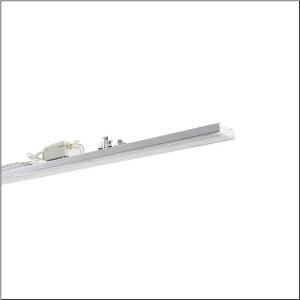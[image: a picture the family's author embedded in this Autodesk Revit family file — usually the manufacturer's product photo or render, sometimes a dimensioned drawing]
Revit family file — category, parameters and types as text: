
# Revit family: licross_r__21_recessed_ho_52te18cn4c5m_57f1
name_source: partatom
category: Lighting Fixtures
units: mm (PartAtom-declared; Revit-internal decimal feet)

## family parameters
Cut with Voids When Loaded = No
Host = Face
Light Source = No
Part Type = Normal
Room Calculation Point = No
Round Connector Dimension = Use Diameter
Shared = No

## types (1)
- --- (1 x LED, 12540 lm, 68.4 W, 4000K)
    Apparent Load = 68 VA
    CIE Flux Codes = 75 94 99 100 100
    Color Rendering = 80
    Color Temperature = 4000K
    Default Elevation = 1800 mm
    Description = Licross® 21 Recessed HO, luminaire insert, of sheet steel, galvanised, coil coated, white, length: 1.500mm, width: 66mm, height: 67mm, LED rated luminous flux: 12.540lm, light colour: 840, control gear: ON/OFF Multilumen, CLOi, control gear: ECG Multilumen, with plug, 3-pole, with phase selection, mains connection: 220..240V, AC, 50/60Hz, start of lifetime: 68W, end of service life: 83W, halogen-free wiring, primary light control with lens, of plastic, primary optical cover: cover, of PMMA, light emission: direct distribution, primary light characteristic: symmetric, protection rating (complete): IP54, insulation class (complete): insulation class I (protective earthing), certification: CE, ENEC, VDE, UKCA, protection symbol: D if used in an environment with non-conductive dust loads with corresponding accessories, impact resistance: IK06, permissible ambient temperature for indoor applications: -35..+30°C, corresponds to IFS (International Featured Standards) requirements for safety and quality in the food industry, reducing of maximum allowable ambient temperature of 5°C with ceiling mounting, LABS conformity tested according to VDMA 24364:2018-05, packaging unit: 1 piece
    Height = 58 mm
    Lamp = 1 x LED
    Lamp Light Flux = 12540 lm
    Lamp Power = 68.4 W
    Lamp count = 1
    Length = 1500 mm
    Luminous efficacy = 183 lm/W
    Manufacturer = Siteco
    ModVariant = No
    Model = 52TE18CN4C5M
    Mounting Place = Ceiling
    Mounting Type = Pendant
    Number of Poles = 1
    OnlyDefault = Yes
    Power Factor = 1
    Product Name = Licross® 21 Recessed HO
    Product group = luminaire insert
    ProductGroupID = 901
    Protection Class = Protection class I
    Protection Degree = IP 54
    RLX_Detail_Level = 1
    RLX_Emergency_Light_Flux = 0 lm
    RLX_Emergency_Type = 0
    RLX_Emergency_Type_DB = No
    RlxData = <blob elided: 22369 chars, md5=8824ea5e>
    Socket = socket
    Standby Power = 0 W
    System Light Flux = 12540 lm
    System Power = 68 W
    Type Comments = factory setting: luminous flux: 100 % | (A | C | E) | 161 mA
    Type Image = l_1296930.jpg
    URL = http://relux.com
    VarID = @adj_040113
    Voltage = 0 V
    Weight = 0.00 kg
    Width = 66 mm

## geometry (parser evidence)
native form markers: Blend x4, Sweep x12
no freeform markers — native parametric forms only
